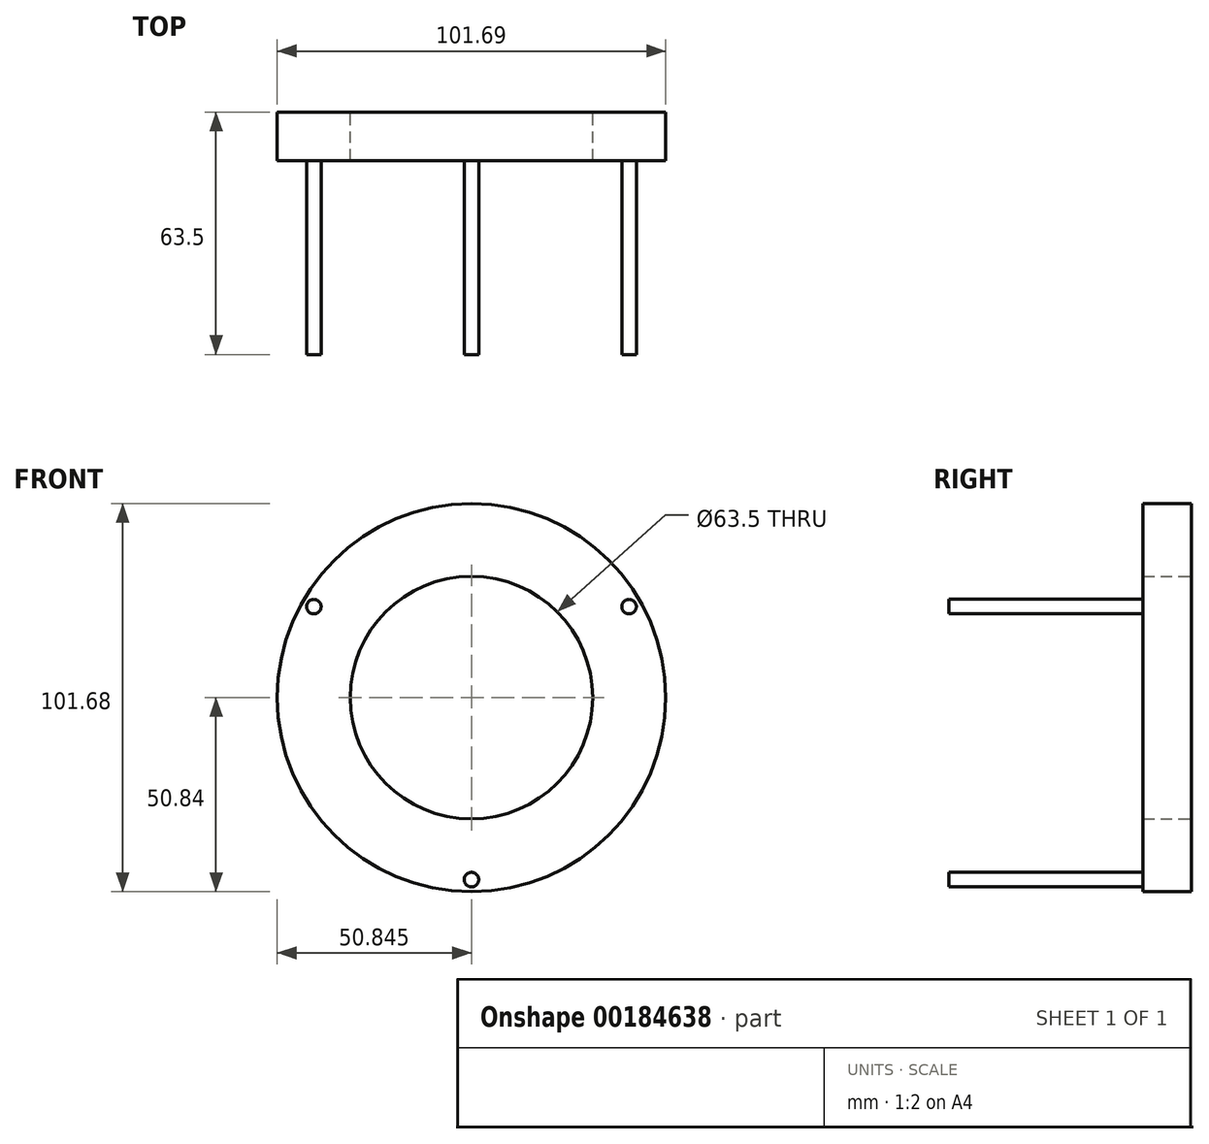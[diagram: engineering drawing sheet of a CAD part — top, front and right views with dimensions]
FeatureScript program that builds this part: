
annotation { "Feature Type Name" : "Feature", "Feature Type Description" : "" }
export const myFeature = defineFeature(function(context is Context, id is Id, definition is map)
    precondition{}
    {
        {
            var Q0;
            Q0=qCreatedBy(makeId("Front.planeOp"),FACE);
            var sketch = newSketch(context, id + "F0", { "sketchPlane" : qUnion([Q0])});
            skCircle(sketch, "E0", {"center": v(-61.31, 0.14) * mm, "radius": 31.75 * mm});
            skPoint(sketch, "E1", {"position": v(-102.58, 23.96) * mm});
            skCircle(sketch, "E2", {"center": v(-102.58, 23.96) * mm, "radius": 1.9 * mm});
            skPoint(sketch, "E3", {"position": v(-20.05, 23.96) * mm});
            skPoint(sketch, "E4", {"position": v(-61.31, -47.5) * mm});
            skCircle(sketch, "E5", {"center": v(-61.31, -47.5) * mm, "radius": 1.9 * mm});
            skCircle(sketch, "E6", {"center": v(-20.05, 23.96) * mm, "radius": 1.9 * mm});
            skPoint(sketch, "E7", {"position": v(-111.14, 10.24) * mm});
            skCircle(sketch, "E8", {"center": v(-61.31, 0.14) * mm, "radius": 50.84 * mm});
            skSolve(sketch);
        }
        {
            var Q0;
            Q0=makeQuery(id+"F0.imprint","IMPRINT",FACE,{"disambiguationData":[TD([[makeQuery(id+"F0.imprint","IMPRINT",EDGE,{"derivedFrom":sQuery(id+"F0.wireOp",EDGE,"E0")}),-1.0]])]});
            extrude(context, id + "F1", {"entities" : qUnion([Q0]), "depth" : 12.7 * mm});
        }
        {
            var Q0;
            Q0=makeQuery(id+"F0.imprint","IMPRINT",FACE,{"disambiguationData":[TD([[makeQuery(id+"F0.imprint","IMPRINT",EDGE,{"derivedFrom":sQuery(id+"F0.wireOp",EDGE,"E2")}),1.0]])]});
            var Q1;
            Q1=makeQuery(id+"F0.imprint","IMPRINT",FACE,{"disambiguationData":[TD([[makeQuery(id+"F0.imprint","IMPRINT",EDGE,{"derivedFrom":sQuery(id+"F0.wireOp",EDGE,"E6")}),1.0]])]});
            var Q2;
            Q2=makeQuery(id+"F0.imprint","IMPRINT",FACE,{"disambiguationData":[TD([[makeQuery(id+"F0.imprint","IMPRINT",EDGE,{"derivedFrom":sQuery(id+"F0.wireOp",EDGE,"E5")}),1.0]])]});
            extrude(context, id + "F2", {"entities" : qUnion([Q0, Q1, Q2]), "operationType" : NewBodyOperationType.ADD, "depth" : 63.5 * mm});
        }
    });
